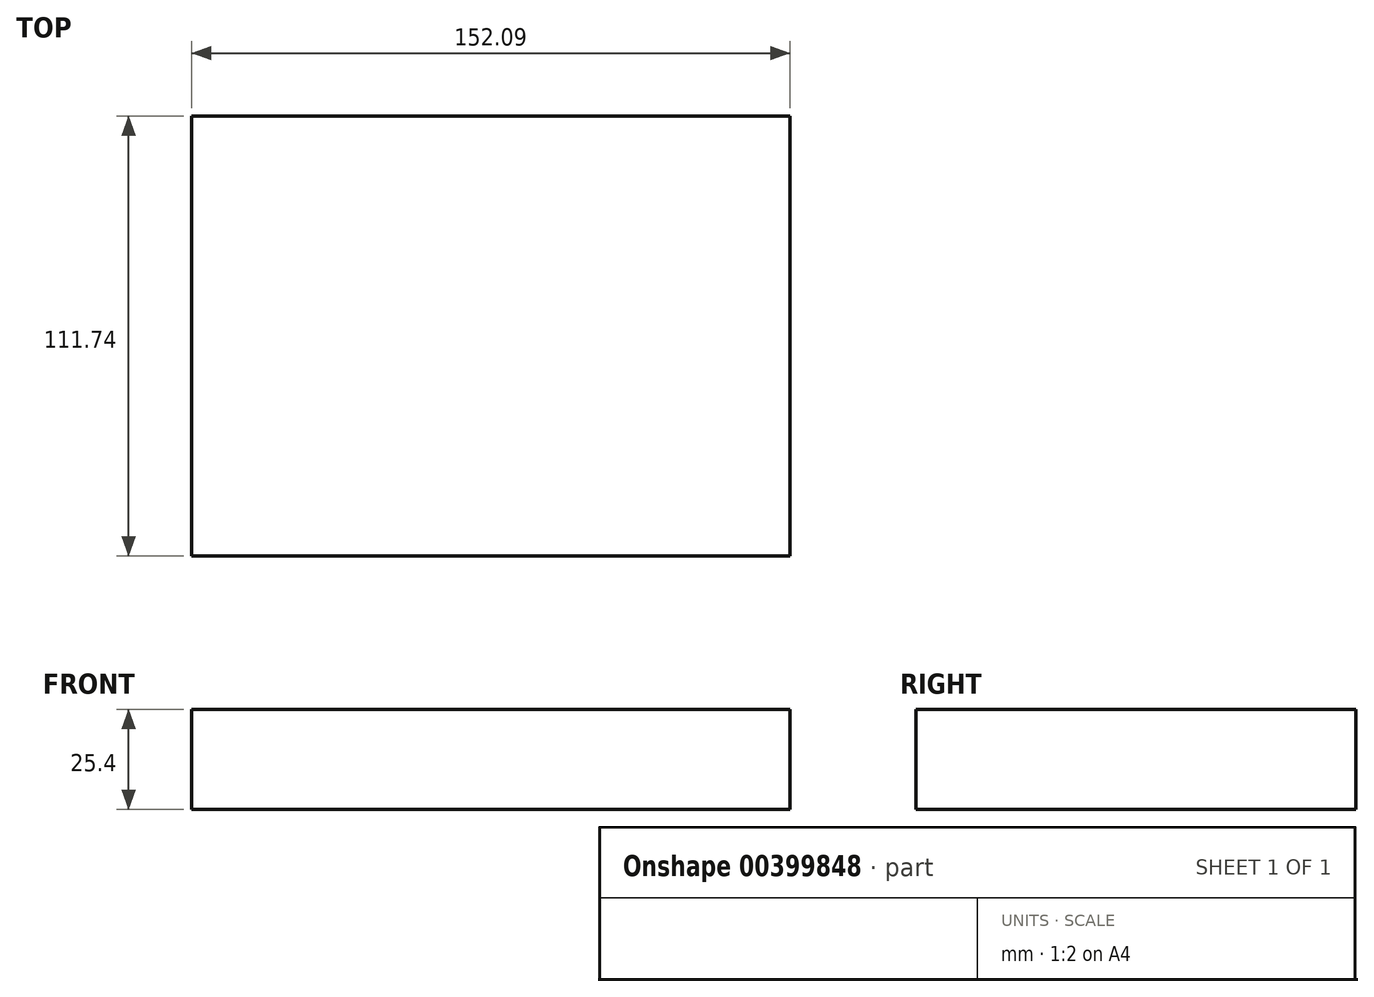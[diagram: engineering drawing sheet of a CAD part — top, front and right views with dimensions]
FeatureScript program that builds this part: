
annotation { "Feature Type Name" : "Feature", "Feature Type Description" : "" }
export const myFeature = defineFeature(function(context is Context, id is Id, definition is map)
    precondition{}
    {
        {
            var Q0;
            Q0=qCreatedBy(makeId("Top.planeOp"),FACE);
            var sketch = newSketch(context, id + "F0", { "sketchPlane" : qUnion([Q0])});
            skLineSegment(sketch, "E0.bottom", {"start": v(-76.22, 55.87) * mm, "end": v(75.87, 55.87) * mm});
            skLineSegment(sketch, "E0.top", {"start": v(-76.22, -55.87) * mm, "end": v(75.87, -55.87) * mm});
            skLineSegment(sketch, "E0.left", {"start": v(-76.22, 55.87) * mm, "end": v(-76.22, -55.87) * mm});
            skLineSegment(sketch, "E0.right", {"start": v(75.87, 55.87) * mm, "end": v(75.87, -55.87) * mm});
            skSolve(sketch);
        }
        {
            var Q0;
            Q0 = qSketchRegion(id + "F0", true);
            extrude(context, id + "F1", {"entities" : qUnion([Q0]), "depth" : 25.4 * mm});
        }
    });
